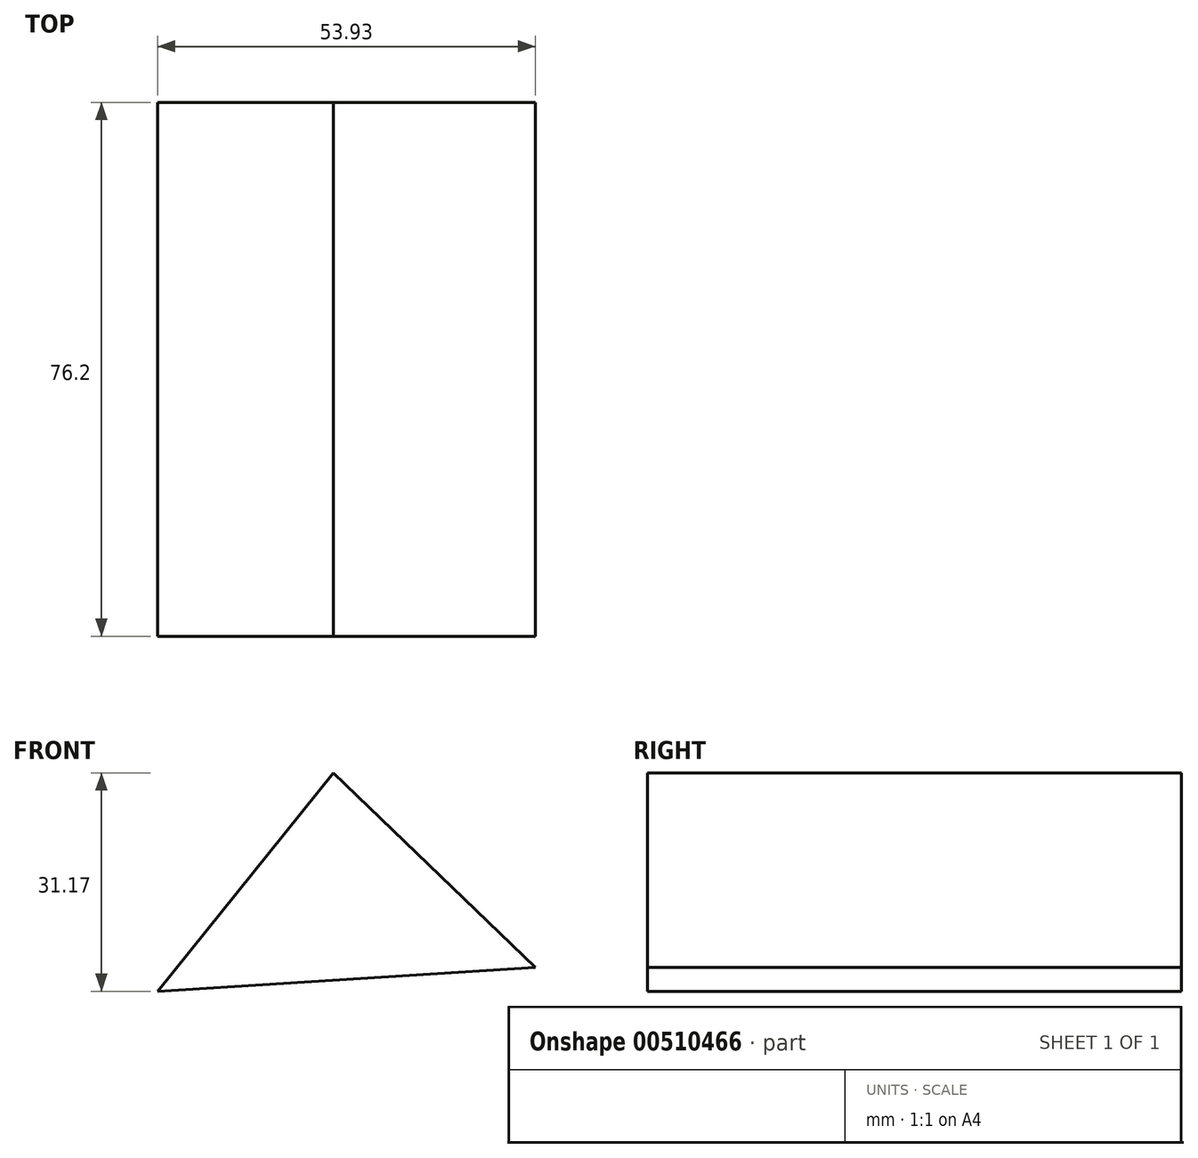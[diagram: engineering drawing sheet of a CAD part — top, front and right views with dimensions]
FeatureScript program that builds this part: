
annotation { "Feature Type Name" : "Feature", "Feature Type Description" : "" }
export const myFeature = defineFeature(function(context is Context, id is Id, definition is map)
    precondition{}
    {
        {
            var Q0;
            Q0=qCreatedBy(makeId("Front.planeOp"),FACE);
            var sketch = newSketch(context, id + "F0", { "sketchPlane" : qUnion([Q0])});
            skLineSegment(sketch, "E0", {"start": v(-25.8, -3.43) * mm, "end": v(-0.7, 27.74) * mm});
            skLineSegment(sketch, "E1", {"start": v(-0.7, 27.74) * mm, "end": v(28.14, 0) * mm});
            skLineSegment(sketch, "E2", {"start": v(28.14, 0) * mm, "end": v(-25.8, -3.43) * mm});
            skSolve(sketch);
        }
        {
            var Q0;
            Q0=makeQuery(id+"F0.imprint","IMPRINT",FACE,{"disambiguationData":[TD([[makeQuery(id+"F0.imprint","IMPRINT",EDGE,{"derivedFrom":sQuery(id+"F0.wireOp",EDGE,"E0")}),-1.0]])]});
            extrude(context, id + "F1", {"entities" : qUnion([Q0]), "depth" : 76.2 * mm});
        }
    });
